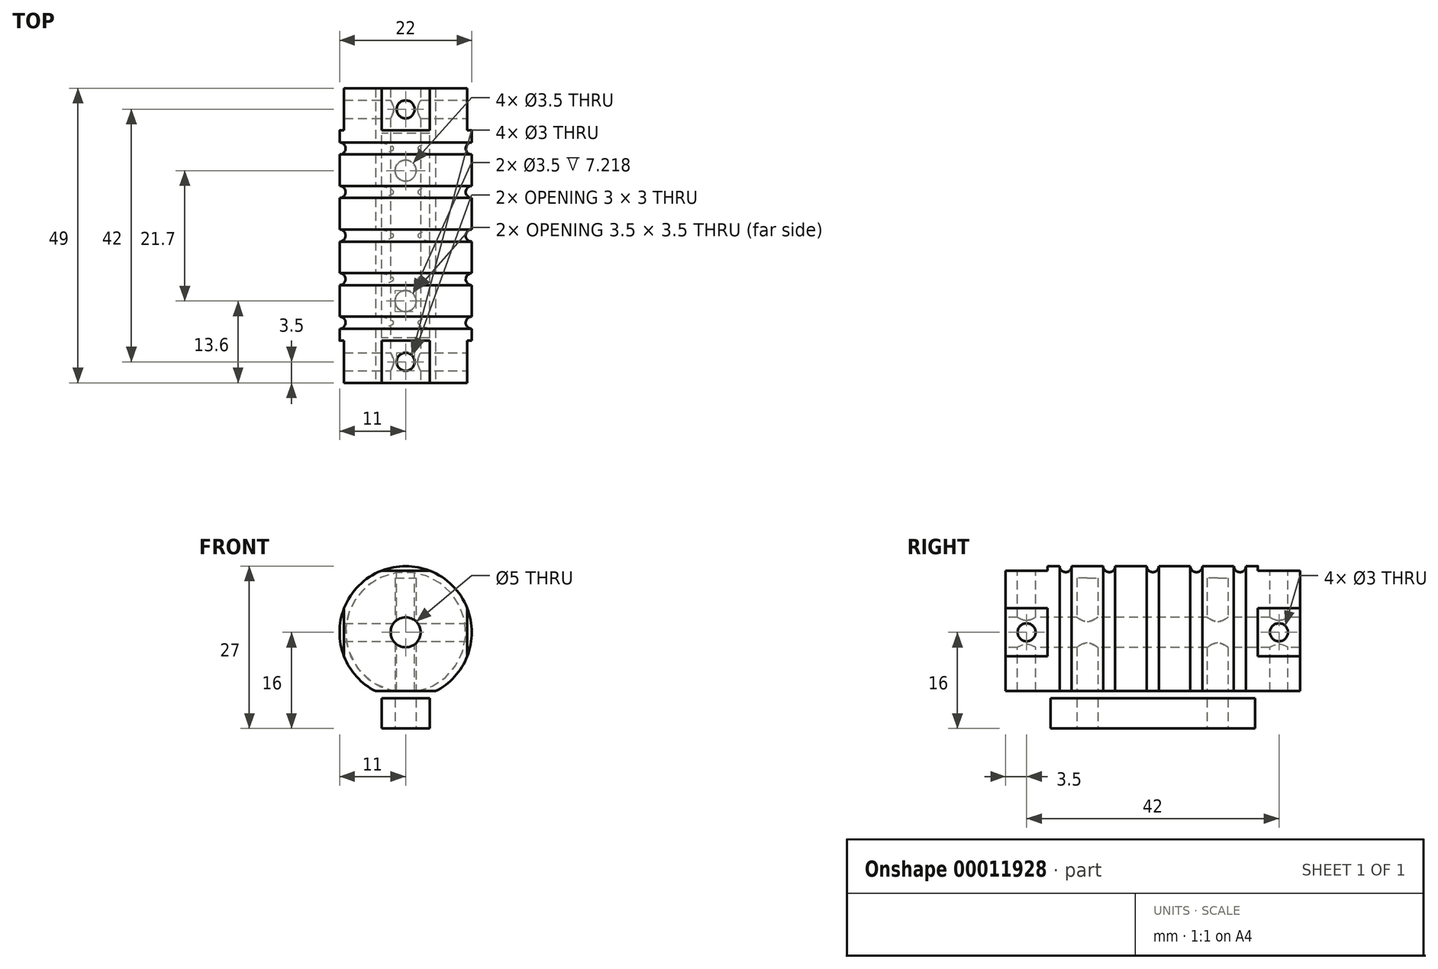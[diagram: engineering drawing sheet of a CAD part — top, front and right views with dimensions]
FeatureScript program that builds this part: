
annotation { "Feature Type Name" : "Feature", "Feature Type Description" : "" }
export const myFeature = defineFeature(function(context is Context, id is Id, definition is map)
    precondition{}
    {
        {
            var Q0;
            Q0=qCreatedBy(makeId("Front.planeOp"),FACE);
            var sketch = newSketch(context, id + "F0", { "sketchPlane" : qUnion([Q0])});
            skCircle(sketch, "E0", {"center": v(0, 0) * mm, "radius": 11 * mm});
            skSolve(sketch);
        }
        {
            var Q0;
            Q0=makeQuery(id+"F0.imprint","IMPRINT",FACE,{"disambiguationData":[TD([[makeQuery(id+"F0.imprint","IMPRINT",EDGE,{"derivedFrom":sQuery(id+"F0.wireOp",EDGE,"E0")}),1.0]])]});
            extrude(context, id + "F1", {"entities" : qUnion([Q0]), "depth" : 49 * mm});
        }
        {
            var Q0;
            Q0=makeQuery(id+"F1.opExtrude","CAP_FACE",FACE,{"disambiguationData":[OSD([sQuery(id+"F0.wireOp",EDGE,"E0")])],"isStart":false});
            var sketch = newSketch(context, id + "F2", { "sketchPlane" : qUnion([Q0])});
            skCircle(sketch, "E1", {"center": v(0, 0) * mm, "radius": 2.5 * mm});
            skSolve(sketch);
        }
        {
            var Q0;
            Q0=qSketchRegion(id+"F2",true);
            extrude(context, id + "F3", {"entities" : qUnion([Q0]), "operationType" : NewBodyOperationType.REMOVE, "endBound" : BoundingType.THROUGH_ALL, "oppositeDirection" : true, "depth" : 25 * mm});
        }
        {
            var Q0;
            Q0=qCreatedBy(makeId("Right.planeOp"),FACE);
            var sketch = newSketch(context, id + "F4", { "sketchPlane" : qUnion([Q0])});
            skArc(sketch, "E2", {"start": v(-40, 11) * mm, "mid": v(-39, 10) * mm, "end": v(-38, 11) * mm});
            skLineSegment(sketch, "E3", {"start": v(-39, 11) * mm, "end": v(-39, 10) * mm, "construction": true});
            skLineSegment(sketch, "E4", {"start": v(-40, 11) * mm, "end": v(-40, 12.53) * mm});
            skLineSegment(sketch, "E5", {"start": v(-40, 12.53) * mm, "end": v(-38, 12.53) * mm});
            skLineSegment(sketch, "E6", {"start": v(-38, 12.53) * mm, "end": v(-38, 11) * mm});
            skLineSegment(sketch, "E7.1.0.0", {"start": v(-32.75, 12.53) * mm, "end": v(-30.75, 12.53) * mm});
            skLineSegment(sketch, "E7.1.0.1", {"start": v(-32.75, 11) * mm, "end": v(-32.75, 12.53) * mm});
            skLineSegment(sketch, "E7.1.0.2", {"start": v(-31.75, 11) * mm, "end": v(-31.75, 10) * mm, "construction": true});
            skLineSegment(sketch, "E7.1.0.3", {"start": v(-30.75, 12.53) * mm, "end": v(-30.75, 11) * mm});
            skArc(sketch, "E7.1.0.4", {"start": v(-32.75, 11) * mm, "mid": v(-31.75, 10) * mm, "end": v(-30.75, 11) * mm});
            skLineSegment(sketch, "E7.2.0.0", {"start": v(-25.5, 12.53) * mm, "end": v(-23.5, 12.53) * mm});
            skLineSegment(sketch, "E7.2.0.1", {"start": v(-25.5, 11) * mm, "end": v(-25.5, 12.53) * mm});
            skLineSegment(sketch, "E7.2.0.2", {"start": v(-24.5, 11) * mm, "end": v(-24.5, 10) * mm, "construction": true});
            skLineSegment(sketch, "E7.2.0.3", {"start": v(-23.5, 12.53) * mm, "end": v(-23.5, 11) * mm});
            skArc(sketch, "E7.2.0.4", {"start": v(-25.5, 11) * mm, "mid": v(-24.5, 10) * mm, "end": v(-23.5, 11) * mm});
            skLineSegment(sketch, "E7.3.0.0", {"start": v(-18.25, 12.53) * mm, "end": v(-16.25, 12.53) * mm});
            skLineSegment(sketch, "E7.3.0.1", {"start": v(-18.25, 11) * mm, "end": v(-18.25, 12.53) * mm});
            skLineSegment(sketch, "E7.3.0.2", {"start": v(-17.25, 11) * mm, "end": v(-17.25, 10) * mm, "construction": true});
            skLineSegment(sketch, "E7.3.0.3", {"start": v(-16.25, 12.53) * mm, "end": v(-16.25, 11) * mm});
            skArc(sketch, "E7.3.0.4", {"start": v(-18.25, 11) * mm, "mid": v(-17.25, 10) * mm, "end": v(-16.25, 11) * mm});
            skLineSegment(sketch, "E7.4.0.0", {"start": v(-11, 12.53) * mm, "end": v(-9, 12.53) * mm});
            skLineSegment(sketch, "E7.4.0.1", {"start": v(-11, 11) * mm, "end": v(-11, 12.53) * mm});
            skLineSegment(sketch, "E7.4.0.2", {"start": v(-10, 11) * mm, "end": v(-10, 10) * mm, "construction": true});
            skLineSegment(sketch, "E7.4.0.3", {"start": v(-9, 12.53) * mm, "end": v(-9, 11) * mm});
            skArc(sketch, "E7.4.0.4", {"start": v(-11, 11) * mm, "mid": v(-10, 10) * mm, "end": v(-9, 11) * mm});
            skLineSegment(sketch, "E7.direction1", {"start": v(-40, 12.53) * mm, "end": v(-32.75, 12.53) * mm, "construction": true});
            skLineSegment(sketch, "E8", {"start": v(-49, 0) * mm, "end": v(0, 0) * mm, "construction": true});
            skLineSegment(sketch, "E9.0", {"start": v(-49, -11) * mm, "end": v(-49, 11) * mm, "construction": true});
            skSolve(sketch);
        }
        {
            var Q0;
            Q0=qSketchRegion(id+"F4",true);
            var Q1;
            Q1=sQuery(id+"F4.wireOp",EDGE,"E8");
            revolve(context, id + "F5", {"operationType" : NewBodyOperationType.REMOVE, "entities" : qUnion([Q0]), "axis" : qUnion([Q1]), "revolveType" : RevolveType.FULL, "oppositeDirection" : true});
        }
        {
            var Q0;
            Q0=qCreatedBy(makeId("Top.planeOp"),FACE);
            cPlane(context, id + "F6", {"entities" : qUnion([Q0]), "cplaneType" : CPlaneType.OFFSET, "offset" : 16 * mm, "oppositeDirection" : true, "width" : 150 * mm, "height" : 150 * mm});
        }
        {
            var Q0;
            Q0=qCreatedBy(id+"F6.planeOp",FACE);
            var sketch = newSketch(context, id + "F7", { "sketchPlane" : qUnion([Q0])});
            skLineSegment(sketch, "E10", {"start": v(0, 0) * mm, "end": v(0, -49) * mm, "construction": true});
            skLineSegment(sketch, "E11.0", {"start": v(11, -49) * mm, "end": v(-11, -49) * mm, "construction": true});
            skLineSegment(sketch, "E12.rect.bottom", {"start": v(4, -41.5) * mm, "end": v(-4, -41.5) * mm});
            skLineSegment(sketch, "E12.rect.top", {"start": v(4, -7.5) * mm, "end": v(-4, -7.5) * mm});
            skLineSegment(sketch, "E12.rect.left", {"start": v(4, -41.5) * mm, "end": v(4, -7.5) * mm});
            skLineSegment(sketch, "E12.rect.right", {"start": v(-4, -41.5) * mm, "end": v(-4, -7.5) * mm});
            skPoint(sketch, "E12.rect.middle", {"position": v(0, -24.5) * mm});
            skPoint(sketch, "E13", {"position": v(0, -7.5) * mm});
            skSolve(sketch);
        }
        {
            var Q0;
            Q0 = qSketchRegion(id + "F7", true);
            extrude(context, id + "F8", {"entities" : qUnion([Q0]), "depth" : 5 * mm});
        }
        {
            var Q0;
            Q0=qCreatedBy(id+"F6.planeOp",FACE);
            var sketch = newSketch(context, id + "F9", { "sketchPlane" : qUnion([Q0])});
            skCircle(sketch, "E14", {"center": v(0, -35.4) * mm, "radius": 1.75 * mm});
            skCircle(sketch, "E15", {"center": v(0, -13.7) * mm, "radius": 1.75 * mm});
            skLineSegment(sketch, "E16", {"start": v(0, 0) * mm, "end": v(0, -51.54) * mm, "construction": true});
            skSolve(sketch);
        }
        {
            var Q0;
            Q0 = qSketchRegion(id + "F9", true);
            extrude(context, id + "F10", {"entities" : qUnion([Q0]), "operationType" : NewBodyOperationType.REMOVE, "depth" : 25 * mm});
        }
        {
            var Q0;
            Q0=qCreatedBy(makeId("Top.planeOp"),FACE);
            var sketch = newSketch(context, id + "F11", { "sketchPlane" : qUnion([Q0])});
            skCircle(sketch, "E17", {"center": v(0, -45.5) * mm, "radius": 1.5 * mm});
            skLineSegment(sketch, "E18", {"start": v(0, -49) * mm, "end": v(0, 0) * mm});
            skLineSegment(sketch, "E19.0", {"start": v(11, -49) * mm, "end": v(-11, -49) * mm, "construction": true});
            skLineSegment(sketch, "E20", {"start": v(0, -24.5) * mm, "end": v(18.33, -24.5) * mm, "construction": true});
            skCircle(sketch, "E21.0.MirrorC", {"center": v(0, -3.5) * mm, "radius": 1.5 * mm});
            skSolve(sketch);
        }
        {
            var Q0;
            Q0 = qSketchRegion(id + "F11", true);
            extrude(context, id + "F12", {"entities" : qUnion([Q0]), "operationType" : NewBodyOperationType.REMOVE, "oppositeDirection" : true, "depth" : 25 * mm, "hasSecondDirection" : true, "secondDirectionOppositeDirection" : false, "secondDirectionDepth" : 25 * mm});
        }
        {
            var Q0;
            Q0=makeQuery(id+"F1.opExtrude","CAP_FACE",FACE,{"disambiguationData":[OSD([sQuery(id+"F0.wireOp",EDGE,"E0")])],"isStart":false});
            var sketch = newSketch(context, id + "F13", { "sketchPlane" : qUnion([Q0])});
            skLineSegment(sketch, "E22", {"start": v(4, -10.25) * mm, "end": v(-4, -10.25) * mm});
            skLineSegment(sketch, "E23", {"start": v(4, -10.25) * mm, "end": v(4, -13.02) * mm});
            skLineSegment(sketch, "E24", {"start": v(4, -13.02) * mm, "end": v(-4, -13.02) * mm});
            skLineSegment(sketch, "E25", {"start": v(-4, -13.02) * mm, "end": v(-4, -10.25) * mm});
            skLineSegment(sketch, "E26.1.0", {"start": v(10.25, 4) * mm, "end": v(10.25, -4) * mm});
            skLineSegment(sketch, "E26.1.1", {"start": v(10.25, 4) * mm, "end": v(13.02, 4) * mm});
            skLineSegment(sketch, "E26.1.2", {"start": v(13.02, 4) * mm, "end": v(13.02, -4) * mm});
            skLineSegment(sketch, "E26.1.3", {"start": v(13.02, -4) * mm, "end": v(10.25, -4) * mm});
            skLineSegment(sketch, "E26.2.0", {"start": v(-4, 10.25) * mm, "end": v(4, 10.25) * mm});
            skLineSegment(sketch, "E26.2.1", {"start": v(-4, 10.25) * mm, "end": v(-4, 13.02) * mm});
            skLineSegment(sketch, "E26.2.2", {"start": v(-4, 13.02) * mm, "end": v(4, 13.02) * mm});
            skLineSegment(sketch, "E26.2.3", {"start": v(4, 13.02) * mm, "end": v(4, 10.25) * mm});
            skLineSegment(sketch, "E26.3.0", {"start": v(-10.25, -4) * mm, "end": v(-10.25, 4) * mm});
            skLineSegment(sketch, "E26.3.1", {"start": v(-10.25, -4) * mm, "end": v(-13.02, -4) * mm});
            skLineSegment(sketch, "E26.3.2", {"start": v(-13.02, -4) * mm, "end": v(-13.02, 4) * mm});
            skLineSegment(sketch, "E26.3.3", {"start": v(-13.02, 4) * mm, "end": v(-10.25, 4) * mm});
            skPoint(sketch, "E26.center", {"position": v(0, 0) * mm});
            skSolve(sketch);
        }
        {
            var Q0;
            Q0 = qSketchRegion(id + "F13", true);
            extrude(context, id + "F14", {"entities" : qUnion([Q0]), "operationType" : NewBodyOperationType.REMOVE, "oppositeDirection" : true, "depth" : 7 * mm});
        }
        {
            var Q0;
            Q0=qCreatedBy(makeId("Right.planeOp"),FACE);
            var sketch = newSketch(context, id + "F15", { "sketchPlane" : qUnion([Q0])});
            skLineSegment(sketch, "E27.0", {"start": v(-44, -10.25) * mm, "end": v(-47, -10.25) * mm, "construction": true});
            skLineSegment(sketch, "E28", {"start": v(-45.5, -10.25) * mm, "end": v(-45.5, 10.25) * mm, "construction": true});
            skLineSegment(sketch, "E29.0", {"start": v(-47, 10.25) * mm, "end": v(-44, 10.25) * mm, "construction": true});
            skCircle(sketch, "E30", {"center": v(-45.5, 0) * mm, "radius": 1.5 * mm});
            skLineSegment(sketch, "E31.0", {"start": v(-49, -2.5) * mm, "end": v(-49, 2.5) * mm, "construction": true});
            skLineSegment(sketch, "E32", {"start": v(0, 0) * mm, "end": v(-49, 0) * mm, "construction": true});
            skLineSegment(sketch, "E33", {"start": v(-24.5, 0) * mm, "end": v(-24.5, -12.63) * mm, "construction": true});
            skCircle(sketch, "E34.0.MirrorC", {"center": v(-3.5, 0) * mm, "radius": 1.5 * mm});
            skSolve(sketch);
        }
        {
            var Q0;
            Q0 = qSketchRegion(id + "F15", true);
            extrude(context, id + "F16", {"entities" : qUnion([Q0]), "operationType" : NewBodyOperationType.REMOVE, "oppositeDirection" : true, "depth" : 25 * mm, "hasSecondDirection" : true, "secondDirectionOppositeDirection" : false, "secondDirectionDepth" : 25 * mm});
        }
        {
            var Q0;
            Q0=makeQuery(id+"F1.opExtrude","CAP_FACE",FACE,{"disambiguationData":[OSD([sQuery(id+"F0.wireOp",EDGE,"E0")])],"isStart":true});
            var sketch = newSketch(context, id + "F17", { "sketchPlane" : qUnion([Q0])});
            skLineSegment(sketch, "E35", {"start": v(4, -10.25) * mm, "end": v(-4, -10.25) * mm});
            skPoint(sketch, "E36", {"position": v(0, -10.25) * mm});
            skLineSegment(sketch, "E37", {"start": v(4, -10.25) * mm, "end": v(4, -12.35) * mm});
            skLineSegment(sketch, "E38", {"start": v(4, -12.35) * mm, "end": v(-4, -12.35) * mm});
            skLineSegment(sketch, "E39", {"start": v(-4, -12.35) * mm, "end": v(-4, -10.25) * mm});
            skLineSegment(sketch, "E40.1.0", {"start": v(10.25, 4) * mm, "end": v(12.35, 4) * mm});
            skLineSegment(sketch, "E40.1.1", {"start": v(12.35, 4) * mm, "end": v(12.35, -4) * mm});
            skPoint(sketch, "E40.1.2", {"position": v(10.25, 0) * mm});
            skLineSegment(sketch, "E40.1.3", {"start": v(12.35, -4) * mm, "end": v(10.25, -4) * mm});
            skLineSegment(sketch, "E40.1.4", {"start": v(10.25, 4) * mm, "end": v(10.25, -4) * mm});
            skLineSegment(sketch, "E40.2.0", {"start": v(-4, 10.25) * mm, "end": v(-4, 12.35) * mm});
            skLineSegment(sketch, "E40.2.1", {"start": v(-4, 12.35) * mm, "end": v(4, 12.35) * mm});
            skPoint(sketch, "E40.2.2", {"position": v(0, 10.25) * mm});
            skLineSegment(sketch, "E40.2.3", {"start": v(4, 12.35) * mm, "end": v(4, 10.25) * mm});
            skLineSegment(sketch, "E40.2.4", {"start": v(-4, 10.25) * mm, "end": v(4, 10.25) * mm});
            skLineSegment(sketch, "E40.3.0", {"start": v(-10.25, -4) * mm, "end": v(-12.35, -4) * mm});
            skLineSegment(sketch, "E40.3.1", {"start": v(-12.35, -4) * mm, "end": v(-12.35, 4) * mm});
            skPoint(sketch, "E40.3.2", {"position": v(-10.25, 0) * mm});
            skLineSegment(sketch, "E40.3.3", {"start": v(-12.35, 4) * mm, "end": v(-10.25, 4) * mm});
            skLineSegment(sketch, "E40.3.4", {"start": v(-10.25, -4) * mm, "end": v(-10.25, 4) * mm});
            skPoint(sketch, "E40.center", {"position": v(0, 0) * mm});
            skSolve(sketch);
        }
        {
            var Q0;
            Q0 = qSketchRegion(id + "F17", true);
            extrude(context, id + "F18", {"entities" : qUnion([Q0]), "operationType" : NewBodyOperationType.REMOVE, "oppositeDirection" : true, "depth" : 7 * mm});
        }
        {
            var Q0;
            Q0=makeQuery(id+"F1.opExtrude","CAP_FACE",FACE,{"disambiguationData":[OSD([sQuery(id+"F0.wireOp",EDGE,"E0")])],"isStart":false});
            var sketch = newSketch(context, id + "F19", { "sketchPlane" : qUnion([Q0])});
            skLineSegment(sketch, "E41", {"start": v(-5, -9.8) * mm, "end": v(5, -9.8) * mm});
            skArc(sketch, "E42.0", {"start": v(4, -10.25) * mm, "mid": v(4.5, -10.03) * mm, "end": v(5, -9.8) * mm});
            skArc(sketch, "E43.0", {"start": v(-4, -10.25) * mm, "mid": v(0, -11) * mm, "end": v(4, -10.25) * mm});
            skArc(sketch, "E44.0", {"start": v(-5, -9.8) * mm, "mid": v(-4.5, -10.03) * mm, "end": v(-4, -10.25) * mm});
            skPoint(sketch, "E45.orphan", {"position": v(-10.25, -4) * mm});
            skPoint(sketch, "E46.orphan", {"position": v(10.25, -4) * mm});
            skSolve(sketch);
        }
        {
            var Q0;
            Q0 = qSketchRegion(id + "F19", true);
            extrude(context, id + "F20", {"entities" : qUnion([Q0]), "operationType" : NewBodyOperationType.REMOVE, "endBound" : BoundingType.THROUGH_ALL, "oppositeDirection" : true, "depth" : 25 * mm});
        }
    });
